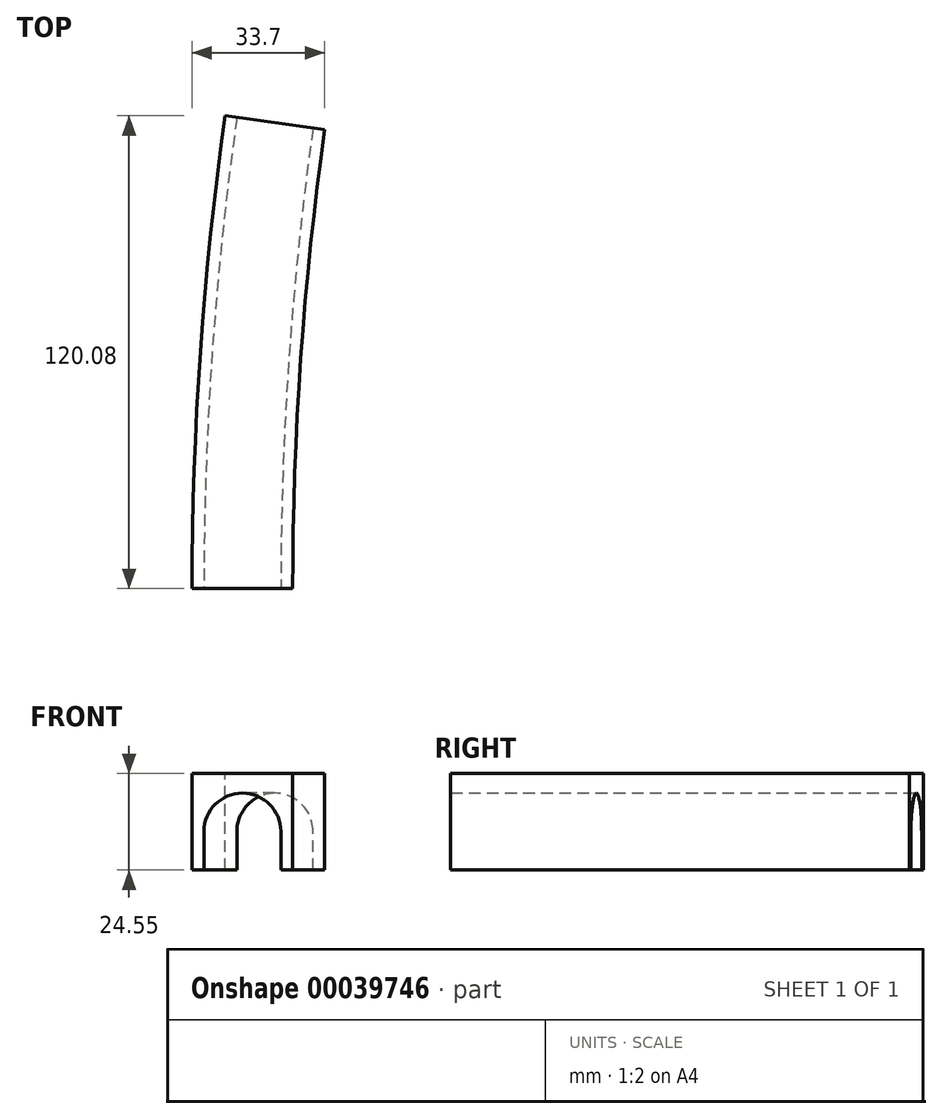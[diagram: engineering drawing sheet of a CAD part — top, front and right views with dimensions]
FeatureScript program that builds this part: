
annotation { "Feature Type Name" : "Feature", "Feature Type Description" : "" }
export const myFeature = defineFeature(function(context is Context, id is Id, definition is map)
    precondition{}
    {
        {
            var Q0;
            Q0=qCreatedBy(makeId("Front.planeOp"),FACE);
            var sketch = newSketch(context, id + "F0", { "sketchPlane" : qUnion([Q0])});
            skArc(sketch, "E0", {"start": v(9.78, 9.78) * mm, "mid": v(0, 19.55) * mm, "end": v(-9.78, 9.78) * mm});
            skLineSegment(sketch, "E1", {"start": v(-9.78, 0) * mm, "end": v(-9.78, 9.78) * mm});
            skLineSegment(sketch, "E2", {"start": v(9.78, 0) * mm, "end": v(9.78, 9.78) * mm});
            skLineSegment(sketch, "E3", {"start": v(-9.78, 0) * mm, "end": v(-12.78, 0) * mm});
            skLineSegment(sketch, "E4", {"start": v(-12.78, 0) * mm, "end": v(-12.78, 24.55) * mm});
            skLineSegment(sketch, "E5", {"start": v(-12.78, 24.55) * mm, "end": v(12.78, 24.55) * mm});
            skLineSegment(sketch, "E6", {"start": v(12.78, 24.55) * mm, "end": v(12.78, 0) * mm});
            skLineSegment(sketch, "E7", {"start": v(12.78, 0) * mm, "end": v(9.78, 0) * mm});
            skSolve(sketch);
        }
        {
            var Q0;
            Q0=qCreatedBy(makeId("Top.planeOp"),FACE);
            var sketch = newSketch(context, id + "F1", { "sketchPlane" : qUnion([Q0])});
            skArc(sketch, "E8", {"start": v(8.27, 118.3) * mm, "mid": v(2.07, 59.3) * mm, "end": v(0, 0) * mm});
            skLineSegment(sketch, "E9", {"start": v(8.27, 118.3) * mm, "end": v(850, 0) * mm, "construction": true});
            skLineSegment(sketch, "E10", {"start": v(0, 0) * mm, "end": v(850, 0) * mm, "construction": true});
            skSolve(sketch);
        }
        {
            var Q0;
            Q0 = qSketchRegion(id + "F0", true);
            var Q1;
            Q1=sQuery(id+"F1.wireOp",EDGE,"E8");
            sweep(context, id + "F2", {"profiles" : qUnion([Q0]), "path" : qUnion([Q1])});
        }
    });
